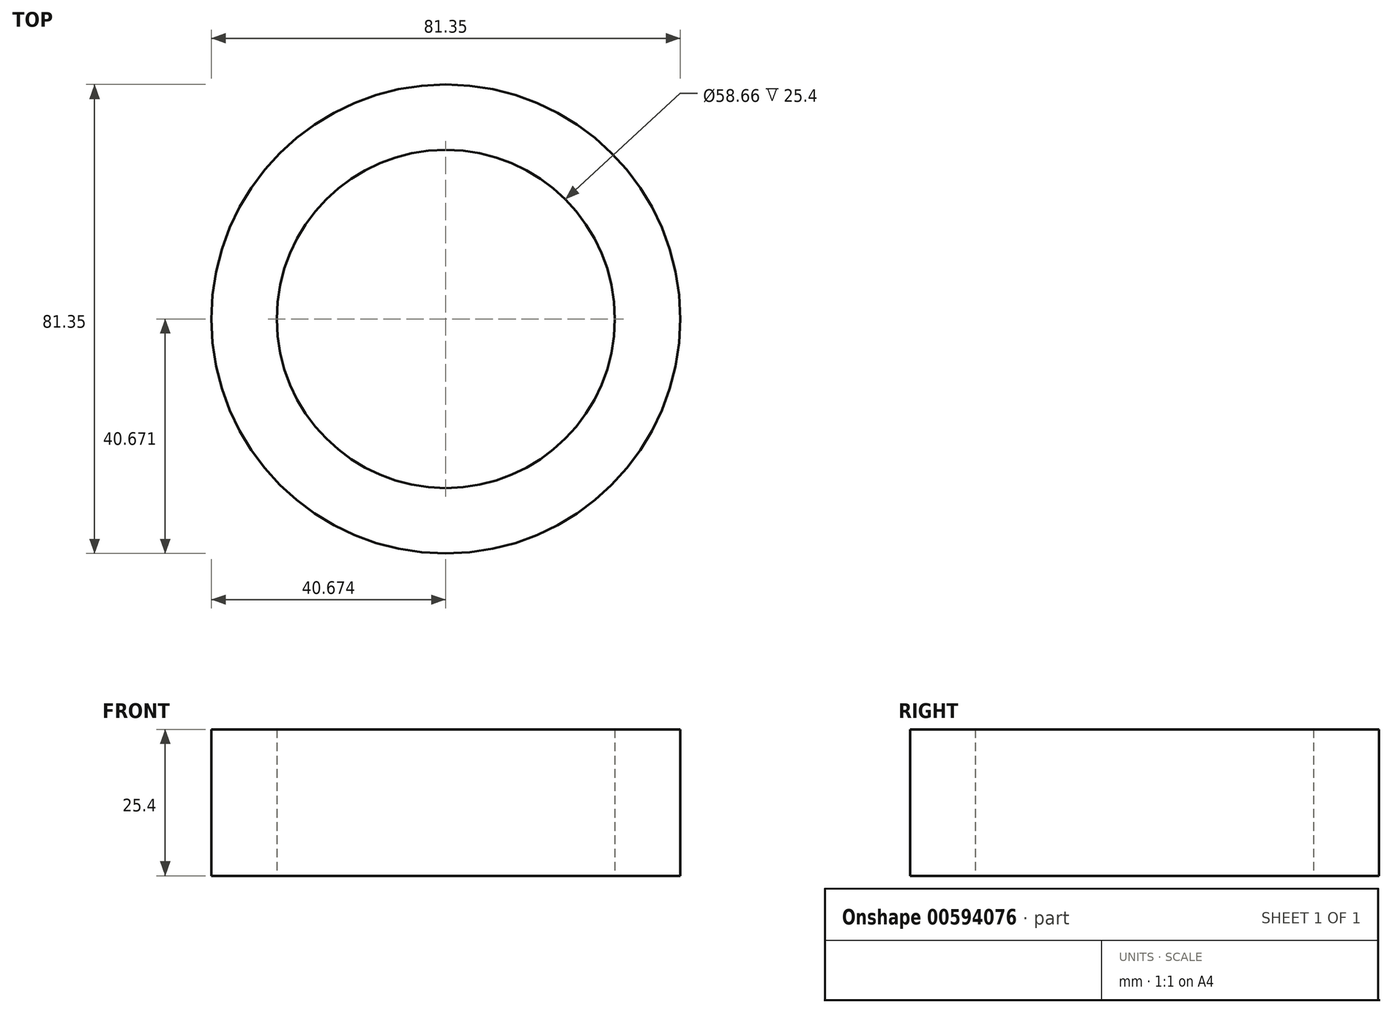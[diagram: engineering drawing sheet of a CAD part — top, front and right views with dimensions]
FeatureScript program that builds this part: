
annotation { "Feature Type Name" : "Feature", "Feature Type Description" : "" }
export const myFeature = defineFeature(function(context is Context, id is Id, definition is map)
    precondition{}
    {
        {
            var Q0;
            Q0=qCreatedBy(makeId("Top.planeOp"),FACE);
            var sketch = newSketch(context, id + "F0", { "sketchPlane" : qUnion([Q0])});
            skCircle(sketch, "E0", {"center": v(-17.6, 20.37) * mm, "radius": 40.68 * mm});
            skCircle(sketch, "E1", {"center": v(-17.6, 20.37) * mm, "radius": 29.33 * mm});
            skCircle(sketch, "E2", {"center": v(-17.6, 20.37) * mm, "radius": 15.4 * mm});
            skSolve(sketch);
        }
        {
            var Q0;
            Q0=makeQuery(id+"F0.imprint","IMPRINT",FACE,{"disambiguationData":[TD([[makeQuery(id+"F0.imprint","IMPRINT",EDGE,{"derivedFrom":sQuery(id+"F0.wireOp",EDGE,"E0")}),1.0]])]});
            extrude(context, id + "F1", {"entities" : qUnion([Q0]), "depth" : 25.4 * mm, "offsetDistance" : 25.4 * mm});
        }
    });
